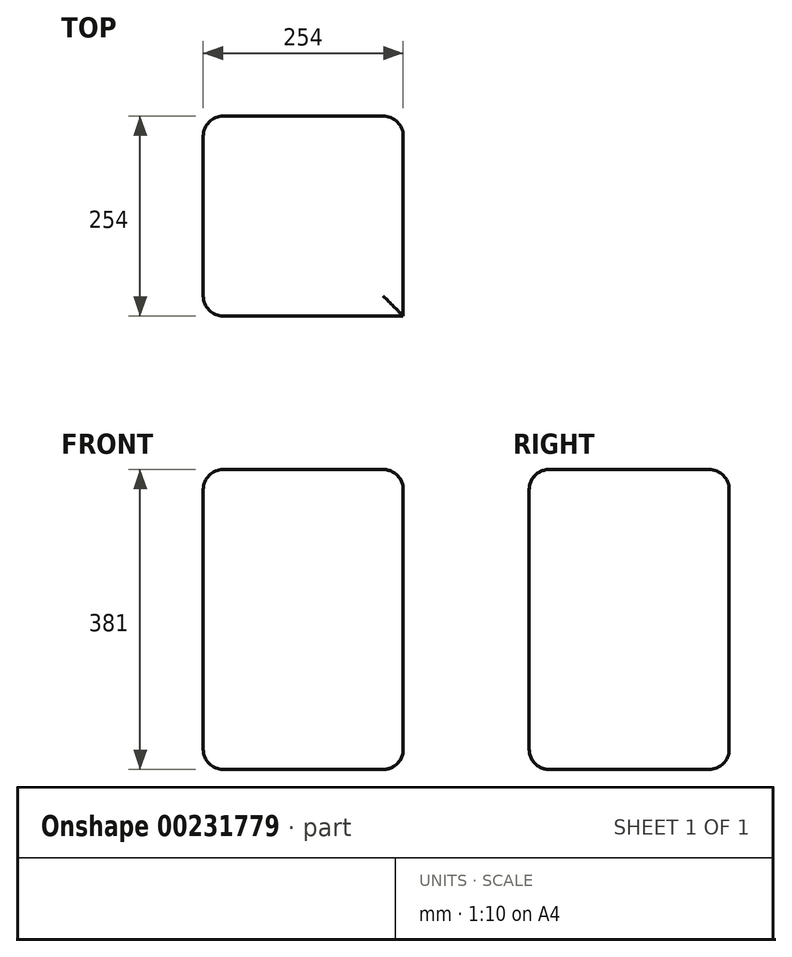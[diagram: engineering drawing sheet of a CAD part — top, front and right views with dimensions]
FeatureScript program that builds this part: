
annotation { "Feature Type Name" : "Feature", "Feature Type Description" : "" }
export const myFeature = defineFeature(function(context is Context, id is Id, definition is map)
    precondition{}
    {
        {
            var Q0;
            Q0=qCreatedBy(makeId("Top.planeOp"),FACE);
            var sketch = newSketch(context, id + "F0", { "sketchPlane" : qUnion([Q0])});
            skLineSegment(sketch, "E0.bottom", {"start": v(-69.39, -40.4) * mm, "end": v(184.61, -40.4) * mm});
            skLineSegment(sketch, "E0.top", {"start": v(-69.39, 213.6) * mm, "end": v(184.61, 213.6) * mm});
            skLineSegment(sketch, "E0.left", {"start": v(-69.39, -40.4) * mm, "end": v(-69.39, 213.6) * mm});
            skLineSegment(sketch, "E0.right", {"start": v(184.61, -40.4) * mm, "end": v(184.61, 213.6) * mm});
            skSolve(sketch);
        }
        {
            var Q0;
            Q0 = qSketchRegion(id + "F0", true);
            extrude(context, id + "F1", {"entities" : qUnion([Q0]), "depth" : 381 * mm});
        }
        {
            var Q0;
            Q0=makeQuery(id+"F1.opExtrude","CAP_FACE",FACE,{"disambiguationData":[OSD([sQuery(id+"F0.wireOp",EDGE,"E0.bottom"),sQuery(id+"F0.wireOp",EDGE,"E0.top"),sQuery(id+"F0.wireOp",EDGE,"E0.left"),sQuery(id+"F0.wireOp",EDGE,"E0.right")])],"isStart":false});
            var Q1;
            Q1=makeQuery(id+"F1.opExtrude","CAP_FACE",FACE,{"disambiguationData":[OSD([sQuery(id+"F0.wireOp",EDGE,"E0.bottom"),sQuery(id+"F0.wireOp",EDGE,"E0.top"),sQuery(id+"F0.wireOp",EDGE,"E0.left"),sQuery(id+"F0.wireOp",EDGE,"E0.right")])],"isStart":true});
            var Q2;
            Q2=makeQuery(id+"F1.opExtrude","SWEPT_FACE",FACE,{"disambiguationData":[OSD([sQuery(id+"F0.wireOp",EDGE,"E0.left")])]});
            var Q3;
            Q3=makeQuery(id+"F1.opExtrude","CAP_EDGE",EDGE,{"disambiguationData":[OSD([sQuery(id+"F0.wireOp",EDGE,"E0.left")])],"isStart":true});
            var Q4;
            Q4=makeQuery(id+"F1.opExtrude","CAP_EDGE",EDGE,{"disambiguationData":[OSD([sQuery(id+"F0.wireOp",EDGE,"E0.left")])],"isStart":false});
            var Q5;
            Q5=makeQuery(id+"F1.opExtrude","SWEPT_EDGE",EDGE,{"disambiguationData":[OSD([sQuery(id+"F0.wireOp",EDGE,"E0.top"),sQuery(id+"F0.wireOp",EDGE,"E0.left")])]});
            var Q6;
            Q6=makeQuery(id+"F1.opExtrude","CAP_EDGE",EDGE,{"disambiguationData":[OSD([sQuery(id+"F0.wireOp",EDGE,"E0.top")])],"isStart":true});
            var Q7;
            Q7=makeQuery(id+"F1.opExtrude","SWEPT_FACE",FACE,{"disambiguationData":[OSD([sQuery(id+"F0.wireOp",EDGE,"E0.top")])]});
            var Q8;
            Q8=makeQuery(id+"F1.opExtrude","CAP_EDGE",EDGE,{"disambiguationData":[OSD([sQuery(id+"F0.wireOp",EDGE,"E0.top")])],"isStart":false});
            fillet(context, id + "F2", {"entities" : qUnion([Q0, Q1, Q2, Q3, Q4, Q5, Q6, Q7, Q8]), "radius" : 25.4 * mm, "tangentPropagation" : true, "allowEdgeOverflow" : false});
        }
    });
